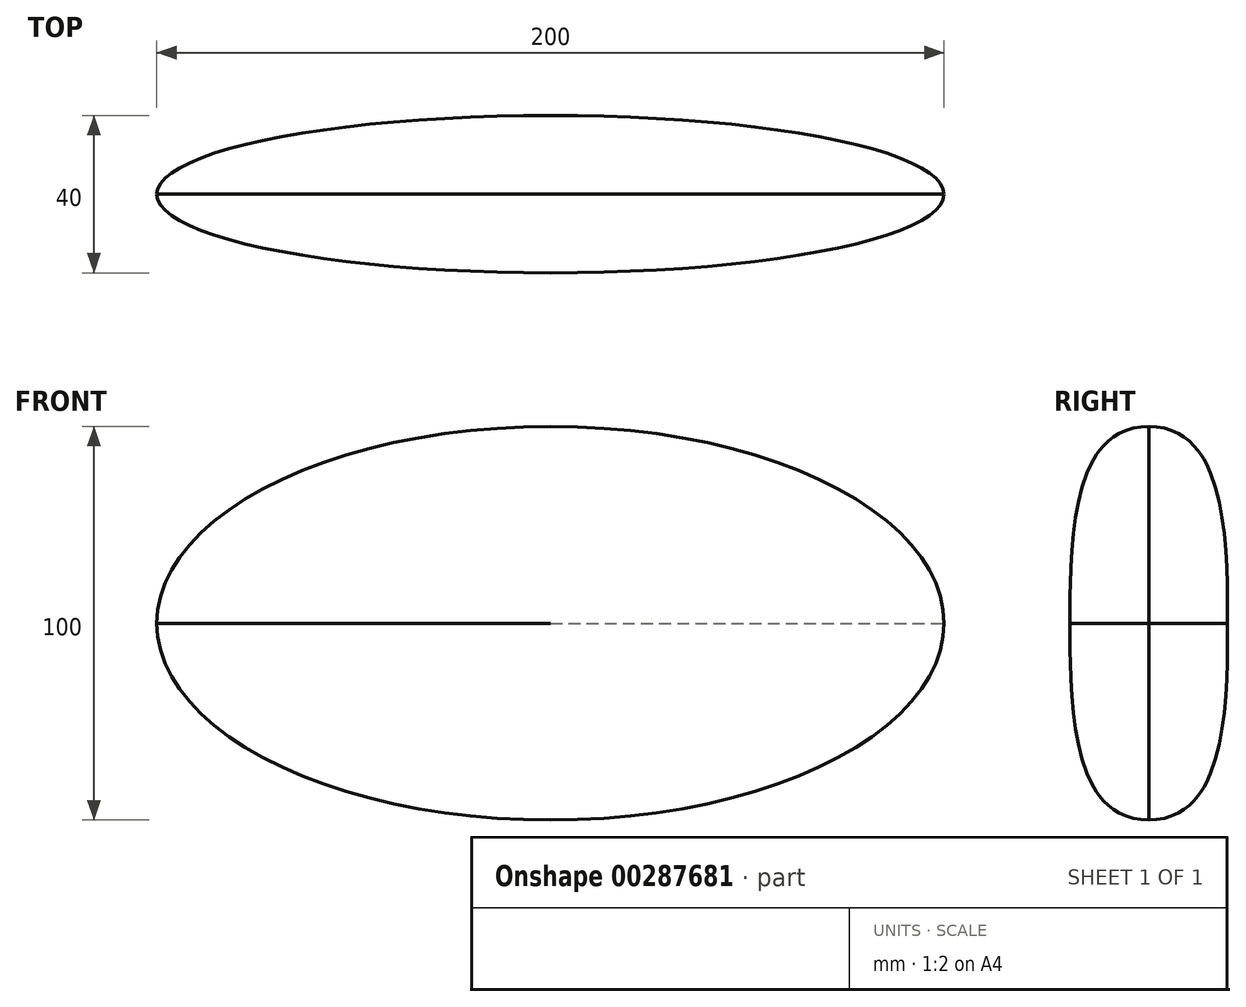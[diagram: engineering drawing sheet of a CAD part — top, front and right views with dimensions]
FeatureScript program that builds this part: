
annotation { "Feature Type Name" : "Feature", "Feature Type Description" : "" }
export const myFeature = defineFeature(function(context is Context, id is Id, definition is map)
    precondition{}
    {
        {
            var Q0;
            Q0=qCreatedBy(makeId("Front.planeOp"),FACE);
            var sketch = newSketch(context, id + "F0", { "sketchPlane" : qUnion([Q0])});
            skLineSegment(sketch, "E0", {"start": v(0, 0) * mm, "end": v(100, 0) * mm, "construction": true});
            skLineSegment(sketch, "E1", {"start": v(0, 0) * mm, "end": v(0, 50) * mm, "construction": true});
            skEllipticalArc(sketch, "E2", {});
            skLineSegment(sketch, "E3", {"start": v(0, 0) * mm, "end": v(-100, 0) * mm, "construction": true});
            const initialGuessF0  = {"E2": [0, 0, 1, 0, 0.1, 0.05, 0, 3.141592653589793]};
            skSetInitialGuess(sketch, initialGuessF0);
            skSolve(sketch);
        }
        {
            var Q0;
            Q0=qCreatedBy(makeId("Top.planeOp"),FACE);
            var sketch = newSketch(context, id + "F1", { "sketchPlane" : qUnion([Q0])});
            skLineSegment(sketch, "E4.0", {"start": v(0, 0) * mm, "end": v(100, 0) * mm});
            skLineSegment(sketch, "E4.1", {"start": v(0, 0) * mm, "end": v(0, 20) * mm});
            skLineSegment(sketch, "E4.3", {"start": v(0, 0) * mm, "end": v(-100, 0) * mm});
            skEllipticalArc(sketch, "E5", {});
            const initialGuessF1  = {"E5": [0, 0, 1, 0, 0.1, 0.02, 0, 3.141592653589793]};
            skSetInitialGuess(sketch, initialGuessF1);
            skSolve(sketch);
        }
        {
            var Q0;
            Q0=qCreatedBy(makeId("Right.planeOp"),FACE);
            var sketch = newSketch(context, id + "F2", { "sketchPlane" : qUnion([Q0])});
            skFitSpline(sketch, "E6", {"points": [v(0, 50) * mm, v(20, 0) * mm], "startDerivative": vector(60, 0) * mm, "endDerivative": vector(0, -60) * mm});
            skLineSegment(sketch, "E7", {"start": v(0, 50) * mm, "end": v(20, 50) * mm});
            skLineSegment(sketch, "E8", {"start": v(20, 0) * mm, "end": v(20, 20) * mm});
            skSolve(sketch);
        }
        {
            var Q0;
            Q0=qSketchRegion(id+"F0",true);
            var Q1;
            Q1=qSketchRegion(id+"F1",true);
            var Q2;
            Q2=sQuery(id+"F0.wireOp",EDGE,"E2");
            var Q3;
            Q3=sQuery(id+"F1.wireOp",EDGE,"E5");
            var Q4;
            Q4=sQuery(id+"F2.wireOp",EDGE,"E6");
            loft(context, id + "F3", {"bodyType" : ToolBodyType.SURFACE, "addGuides" : true, "sheetProfilesArray" : [{ "sheetProfileEntities" : qUnion([Q0]) }, { "sheetProfileEntities" : qUnion([Q1]) }], "wireProfilesArray" : [{ "wireProfileEntities" : qUnion([Q2]) }, { "wireProfileEntities" : qUnion([Q3]) }], "guidesArray" : [{ "guideEntities" : qUnion([Q4]), "guideDerivativeType" : LoftGuideDerivativeType.DEFAULT, "guideDerivativeMagnitude" : 1 }]});
        }
        {
            var Q0;
            Q0=makeQuery(id+"F3.opLoft","SWEPT_BODY",BODY,{"disambiguationData":[OSD([sQuery(id+"F0.wireOp",EDGE,"E2"),sQuery(id+"F1.wireOp",EDGE,"E5"),sQuery(id+"F2.wireOp",EDGE,"E6")])]});
            var Q1;
            Q1=qCreatedBy(makeId("Top.planeOp"),FACE);
            mirror(context, id + "F4", {"entities" : qUnion([Q0]), "mirrorPlane" : qUnion([Q1])});
        }
        {
            var Q0;
            Q0=makeQuery(id+"F3.opLoft","SWEPT_BODY",BODY,{"disambiguationData":[OSD([sQuery(id+"F0.wireOp",EDGE,"E2"),sQuery(id+"F1.wireOp",EDGE,"E5"),sQuery(id+"F2.wireOp",EDGE,"E6")])]});
            var Q1;
            Q1=makeQuery(id+"F4.opPattern","COPY",BODY,{"derivedFrom":makeQuery(id+"F3.opLoft","SWEPT_BODY",BODY,{"disambiguationData":[OSD([sQuery(id+"F0.wireOp",EDGE,"E2"),sQuery(id+"F1.wireOp",EDGE,"E5"),sQuery(id+"F2.wireOp",EDGE,"E6")])]}),"instanceName":"1"});
            var Q2;
            Q2=qCreatedBy(makeId("Front.planeOp"),FACE);
            mirror(context, id + "F5", {"entities" : qUnion([Q0, Q1]), "mirrorPlane" : qUnion([Q2])});
        }
    });
